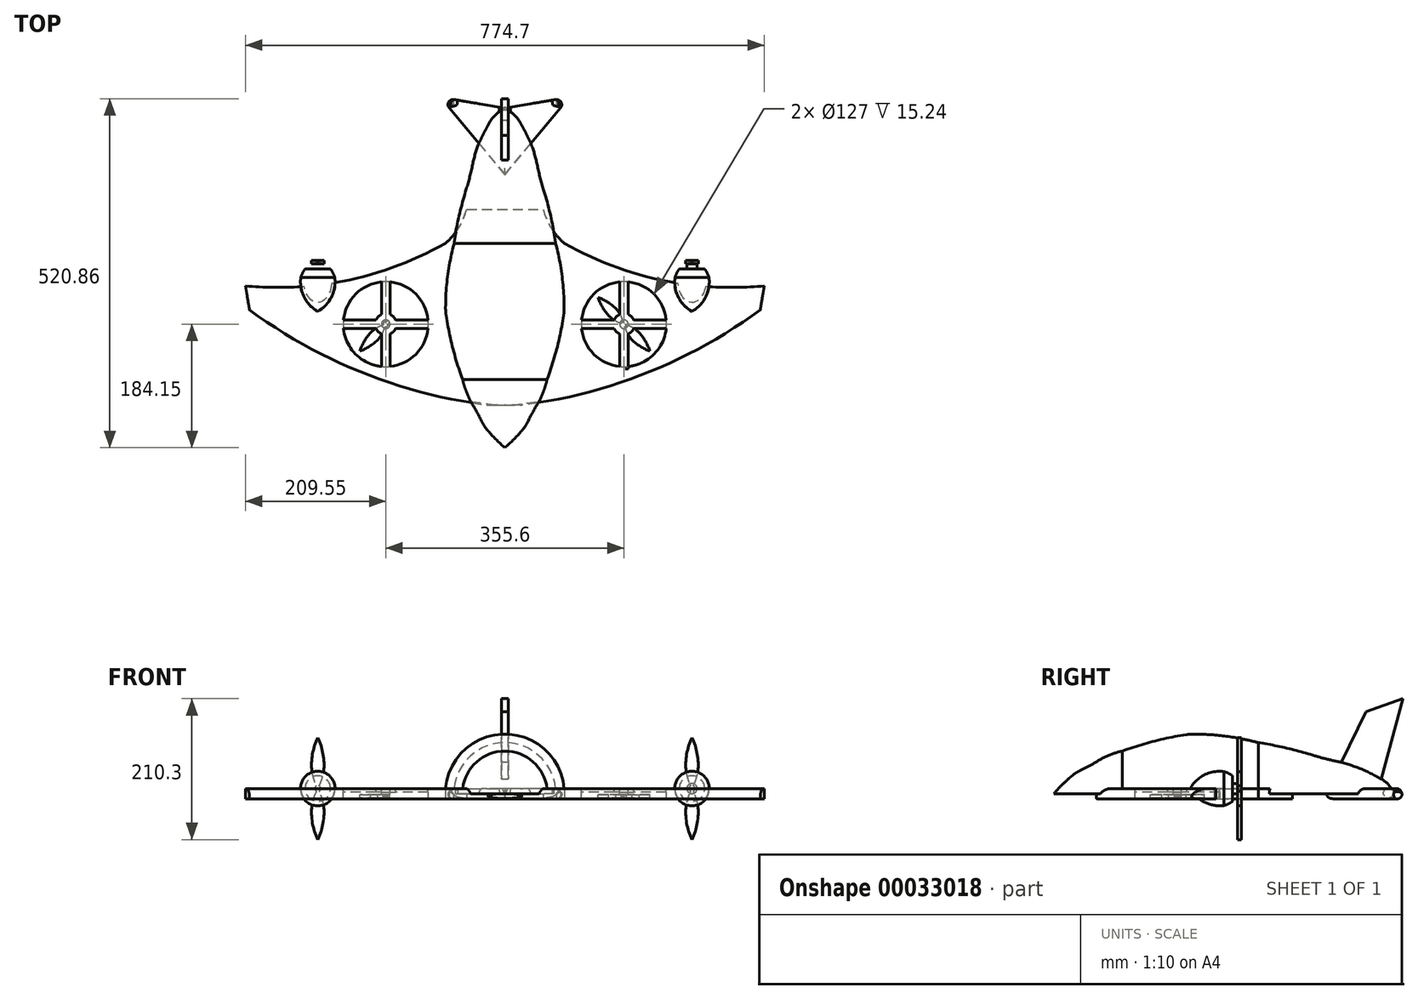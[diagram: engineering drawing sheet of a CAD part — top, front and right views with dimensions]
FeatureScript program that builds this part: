
annotation { "Feature Type Name" : "Feature", "Feature Type Description" : "" }
export const myFeature = defineFeature(function(context is Context, id is Id, definition is map)
    precondition{}
    {
        {
            var Q0;
            Q0=qCreatedBy(makeId("Top.planeOp"),FACE);
            var sketch = newSketch(context, id + "F0", { "sketchPlane" : qUnion([Q0])});
            skPoint(sketch, "E0", {"position": v(0, 304.8) * mm});
            skPoint(sketch, "E1", {"position": v(0, 203.2) * mm});
            skPoint(sketch, "E2", {"position": v(0, 101.6) * mm});
            skPoint(sketch, "E3", {"position": v(0, -101.6) * mm});
            skPoint(sketch, "E4", {"position": v(0, -152.4) * mm});
            skPoint(sketch, "E5", {"position": v(0, -203.2) * mm});
            skPoint(sketch, "E6", {"position": v(-38.1, -152.4) * mm});
            skPoint(sketch, "E7", {"position": v(38.1, -152.4) * mm});
            skPoint(sketch, "E8", {"position": v(-63.5, -101.6) * mm});
            skPoint(sketch, "E9", {"position": v(63.5, -101.6) * mm});
            skPoint(sketch, "E10", {"position": v(-88.9, 0) * mm});
            skPoint(sketch, "E11", {"position": v(88.9, 0) * mm});
            skPoint(sketch, "E12", {"position": v(-76.2, 101.6) * mm});
            skPoint(sketch, "E13", {"position": v(76.2, 101.6) * mm});
            skPoint(sketch, "E14", {"position": v(-50.8, 203.2) * mm});
            skPoint(sketch, "E15", {"position": v(50.8, 203.2) * mm});
            skPoint(sketch, "E16", {"position": v(0, -177.8) * mm});
            skPoint(sketch, "E17", {"position": v(-25.4, -177.8) * mm});
            skPoint(sketch, "E18", {"position": v(25.4, -177.8) * mm});
            skPoint(sketch, "E19", {"position": v(0, 279.4) * mm});
            skPoint(sketch, "E20", {"position": v(-25.4, 279.4) * mm});
            skPoint(sketch, "E21", {"position": v(25.4, 279.4) * mm});
            skArc(sketch, "E22", {"start": v(0, 304.8) * mm, "mid": v(-14.04, 295.38) * mm, "end": v(-24.2, 281.87) * mm});
            skArc(sketch, "E23", {"start": v(24.2, 281.87) * mm, "mid": v(14.04, 295.38) * mm, "end": v(0, 304.8) * mm});
            skArc(sketch, "E24", {"start": v(-27.7, 275.29) * mm, "mid": v(-40, 248.01) * mm, "end": v(-48.17, 219.22) * mm});
            skArc(sketch, "E25", {"start": v(48.17, 219.22) * mm, "mid": v(40, 248.01) * mm, "end": v(27.7, 275.29) * mm});
            skArc(sketch, "E26", {"start": v(-57.48, 183.04) * mm, "mid": v(-68.36, 142.67) * mm, "end": v(-76.2, 101.6) * mm});
            skArc(sketch, "E27", {"start": v(76.2, 101.6) * mm, "mid": v(68.36, 142.67) * mm, "end": v(57.48, 183.04) * mm});
            skArc(sketch, "E28", {"start": v(88.92, 5.93) * mm, "mid": v(85.6, 54.17) * mm, "end": v(76.2, 101.6) * mm});
            skArc(sketch, "E29", {"start": v(-76.2, 101.6) * mm, "mid": v(-85.6, 54.17) * mm, "end": v(-88.92, 5.93) * mm});
            skArc(sketch, "E30", {"start": v(-88.08, -5.72) * mm, "mid": v(-78.26, -54.3) * mm, "end": v(-63.5, -101.6) * mm});
            skArc(sketch, "E31", {"start": v(-23.56, -180.01) * mm, "mid": v(-12.32, -192.16) * mm, "end": v(0, -203.2) * mm});
            skArc(sketch, "E32", {"start": v(63.5, -101.6) * mm, "mid": v(78.26, -54.3) * mm, "end": v(88.08, -5.72) * mm});
            skArc(sketch, "E33", {"start": v(49.61, -136.58) * mm, "mid": v(58, -119.66) * mm, "end": v(63.5, -101.6) * mm});
            skArc(sketch, "E34", {"start": v(-63.5, -101.6) * mm, "mid": v(-58, -119.66) * mm, "end": v(-49.61, -136.58) * mm});
            skArc(sketch, "E35", {"start": v(-33.73, -165.67) * mm, "mid": v(-30.5, -171.31) * mm, "end": v(-26.57, -176.5) * mm});
            skArc(sketch, "E36", {"start": v(0, -203.2) * mm, "mid": v(12.32, -192.16) * mm, "end": v(23.56, -180.01) * mm});
            skArc(sketch, "E37", {"start": v(26.57, -176.5) * mm, "mid": v(30.5, -171.31) * mm, "end": v(33.73, -165.67) * mm});
            skLineSegment(sketch, "E38", {"start": v(0, -203.2) * mm, "end": v(0, 304.8) * mm});
            skArc(sketch, "E39.filletArc", {"start": v(-88.92, 5.93) * mm, "mid": v(-88.72, 0.09) * mm, "end": v(-88.08, -5.72) * mm});
            skArc(sketch, "E40.filletArc", {"start": v(88.08, -5.72) * mm, "mid": v(88.72, 0.09) * mm, "end": v(88.92, 5.93) * mm});
            skArc(sketch, "E41.filletArc", {"start": v(-33.73, -165.67) * mm, "mid": v(-41.35, -150.95) * mm, "end": v(-49.61, -136.58) * mm});
            skArc(sketch, "E42.filletArc", {"start": v(49.61, -136.58) * mm, "mid": v(41.35, -150.95) * mm, "end": v(33.73, -165.67) * mm});
            skArc(sketch, "E43.filletArc", {"start": v(26.57, -176.5) * mm, "mid": v(25.06, -178.25) * mm, "end": v(23.56, -180.01) * mm});
            skArc(sketch, "E44.filletArc", {"start": v(-23.56, -180.01) * mm, "mid": v(-25.06, -178.25) * mm, "end": v(-26.57, -176.5) * mm});
            skArc(sketch, "E45.filletArc", {"start": v(-57.48, 183.04) * mm, "mid": v(-52.38, 201.02) * mm, "end": v(-48.17, 219.22) * mm});
            skArc(sketch, "E46.filletArc", {"start": v(48.17, 219.22) * mm, "mid": v(52.38, 201.02) * mm, "end": v(57.48, 183.04) * mm});
            skArc(sketch, "E47.filletArc", {"start": v(-27.7, 275.29) * mm, "mid": v(-25.93, 278.57) * mm, "end": v(-24.2, 281.87) * mm});
            skArc(sketch, "E48.filletArc", {"start": v(24.2, 281.87) * mm, "mid": v(25.93, 278.57) * mm, "end": v(27.7, 275.29) * mm});
            skSolve(sketch);
        }
        {
            var Q0;
            Q0=makeQuery(id+"F0.imprint","IMPRINT",FACE,{"disambiguationData":[TD([[makeQuery(id+"F0.imprint","IMPRINT",EDGE,{"derivedFrom":sQuery(id+"F0.wireOp",EDGE,"E23")}),1.0]])]});
            var Q1;
            Q1=sQuery(id+"F0.wireOp",EDGE,"E38");
            revolve(context, id + "F1", {"entities" : qUnion([Q0]), "axis" : qUnion([Q1]), "revolveType" : RevolveType.ONE_DIRECTION, "oppositeDirection" : true, "angle" : 180 * degree});
        }
        {
            var Q0;
            Q0=qCreatedBy(makeId("Top.planeOp"),FACE);
            var sketch = newSketch(context, id + "F2", { "sketchPlane" : qUnion([Q0])});
            skPoint(sketch, "E49", {"position": v(-381, 0) * mm});
            skPoint(sketch, "E50", {"position": v(381, 0) * mm});
            skLineSegment(sketch, "E51", {"start": v(0, 0) * mm, "end": v(0, -139.7) * mm});
            skPoint(sketch, "E52", {"position": v(-38.1, -139.7) * mm});
            skPoint(sketch, "E53", {"position": v(38.1, -139.7) * mm});
            skArc(sketch, "E54", {"start": v(-381, 0) * mm, "mid": v(-218.16, -91) * mm, "end": v(-38.1, -139.7) * mm});
            skArc(sketch, "E55", {"start": v(38.1, -139.7) * mm, "mid": v(218.16, -91) * mm, "end": v(381, 0) * mm});
            skLineSegment(sketch, "E56", {"start": v(387.35, 38.1) * mm, "end": v(381, 0) * mm});
            skLineSegment(sketch, "E57", {"start": v(0, 0) * mm, "end": v(0, 152.4) * mm});
            skPoint(sketch, "E58", {"position": v(-57.15, 152.4) * mm});
            skPoint(sketch, "E59", {"position": v(57.15, 152.4) * mm});
            skPoint(sketch, "E60", {"position": v(-88.9, 0) * mm});
            skPoint(sketch, "E61", {"position": v(88.9, 0) * mm});
            skPoint(sketch, "E62", {"position": v(-88.9, 101.6) * mm});
            skPoint(sketch, "E63", {"position": v(88.9, 101.6) * mm});
            skArc(sketch, "E64", {"start": v(-88.9, 101.6) * mm, "mid": v(-69.1, 124.54) * mm, "end": v(-57.15, 152.4) * mm});
            skLineSegment(sketch, "E65", {"start": v(-38.1, -139.7) * mm, "end": v(38.1, -139.7) * mm});
            skLineSegment(sketch, "E66", {"start": v(-57.15, 152.4) * mm, "end": v(57.15, 152.4) * mm});
            skArc(sketch, "E67", {"start": v(57.15, 152.4) * mm, "mid": v(69.2, 124.6) * mm, "end": v(88.9, 101.6) * mm});
            skLineSegment(sketch, "E68", {"start": v(387.35, 0) * mm, "end": v(381, 0) * mm});
            skLineSegment(sketch, "E69", {"start": v(-381, 0) * mm, "end": v(-387.35, 0) * mm});
            skLineSegment(sketch, "E70", {"start": v(-387.35, 38.1) * mm, "end": v(-381, 0) * mm});
            skArc(sketch, "E71", {"start": v(-387.35, 38.1) * mm, "mid": v(-233.24, 46.91) * mm, "end": v(-88.9, 101.6) * mm});
            skArc(sketch, "E72", {"start": v(88.9, 101.6) * mm, "mid": v(233.24, 46.91) * mm, "end": v(387.35, 38.1) * mm});
            skSolve(sketch);
        }
        {
            var Q0;
            Q0 = qSketchRegion(id + "F2", true);
            extrude(context, id + "F3", {"entities" : qUnion([Q0]), "operationType" : NewBodyOperationType.ADD, "endBound" : BoundingType.SYMMETRIC, "depth" : 15.24 * mm});
        }
        {
            var Q0;
            Q0=qCreatedBy(makeId("Right.planeOp"),FACE);
            var sketch = newSketch(context, id + "F4", { "sketchPlane" : qUnion([Q0])});
            skLineSegment(sketch, "E73", {"start": v(0, 0) * mm, "end": v(304.8, 0) * mm});
            skLineSegment(sketch, "E74", {"start": v(0, 0) * mm, "end": v(-203.2, 0) * mm});
            skArc(sketch, "E75", {"start": v(-11.45, 37.92) * mm, "mid": v(-109.64, 30.66) * mm, "end": v(-203.2, 0) * mm});
            skArc(sketch, "E76", {"start": v(304.8, 0) * mm, "mid": v(161.16, 26.9) * mm, "end": v(15.38, 37.11) * mm});
            skPoint(sketch, "E77.visualSharp", {"position": v(0, 37.21) * mm});
            skArc(sketch, "E77.filletArc", {"start": v(-11.45, 37.92) * mm, "mid": v(1.96, 37.4) * mm, "end": v(15.38, 37.11) * mm});
            skSolve(sketch);
        }
        {
            var Q0;
            {var subQ0=sQuery(id+"F2.wireOp",EDGE,"E55");var subQ1=sQuery(id+"F2.wireOp",EDGE,"E56");var subQ2=sQuery(id+"F2.wireOp",EDGE,"E67");var subQ3=sQuery(id+"F2.wireOp",EDGE,"E72");Q0=makeQuery(id+"F3.boolean.opBoolean","SPLIT",FACE,{"disambiguationData":[TD([makeQuery(id+"F3.opExtrude","SWEPT_FACE",FACE,{"disambiguationData":[OSD([subQ0])]})])],"derivedFrom":makeQuery(id+"F3.opExtrude","CAP_FACE",FACE,{"disambiguationData":[OSD([sQuery(id+"F2.wireOp",EDGE,"E54"),subQ0,subQ1,sQuery(id+"F2.wireOp",EDGE,"E64"),sQuery(id+"F2.wireOp",EDGE,"E65"),sQuery(id+"F2.wireOp",EDGE,"E66"),subQ2,sQuery(id+"F2.wireOp",EDGE,"E70"),sQuery(id+"F2.wireOp",EDGE,"E71"),subQ3])],"isStart":false})});}
            cPlane(context, id + "F5", {"entities" : qUnion([Q0]), "cplaneType" : CPlaneType.OFFSET, "offset" : 0 * mm, "width" : 152.4 * mm, "height" : 152.4 * mm});
        }
        {
            var Q0;
            Q0=qCreatedBy(id+"F5.planeOp",FACE);
            var sketch = newSketch(context, id + "F6", { "sketchPlane" : qUnion([Q0])});
            skLineSegment(sketch, "E78", {"start": v(0, 0) * mm, "end": v(0, -19.05) * mm});
            skLineSegment(sketch, "E79", {"start": v(0, -19.05) * mm, "end": v(177.8, -19.05) * mm});
            skLineSegment(sketch, "E80", {"start": v(0, -19.05) * mm, "end": v(-177.8, -19.05) * mm});
            skCircle(sketch, "E81", {"center": v(-177.8, -19.05) * mm, "radius": 63.5 * mm});
            skCircle(sketch, "E82", {"center": v(177.8, -19.05) * mm, "radius": 63.5 * mm});
            skSolve(sketch);
        }
        {
            var Q0;
            Q0=makeQuery(id+"F3.opExtrude","CAP_EDGE",EDGE,{"disambiguationData":[OSD([sQuery(id+"F2.wireOp",EDGE,"E55")])],"isStart":false});
            var Q1;
            Q1=makeQuery(id+"F3.opExtrude","CAP_EDGE",EDGE,{"disambiguationData":[OSD([sQuery(id+"F2.wireOp",EDGE,"E54")])],"isStart":false});
            fillet(context, id + "F7", {"entities" : qUnion([Q0, Q1]), "radius" : 19.05 * mm, "allowEdgeOverflow" : false});
        }
        {
            var Q0;
            {var subQ0=sQuery(id+"F2.wireOp",EDGE,"E54");Q0=makeQuery(id+"F7.opFillet","BLEND_EDGE",EDGE,{"blendedFrom":[makeQuery(id+"F3.opExtrude","CAP_EDGE",EDGE,{"disambiguationData":[OSD([subQ0])],"isStart":false}),makeQuery(id+"F3.opExtrude","CAP_FACE",FACE,{"disambiguationData":[OSD([subQ0,sQuery(id+"F2.wireOp",EDGE,"E55"),sQuery(id+"F2.wireOp",EDGE,"E56"),sQuery(id+"F2.wireOp",EDGE,"E64"),sQuery(id+"F2.wireOp",EDGE,"E65"),sQuery(id+"F2.wireOp",EDGE,"E66"),sQuery(id+"F2.wireOp",EDGE,"E67"),sQuery(id+"F2.wireOp",EDGE,"E70"),sQuery(id+"F2.wireOp",EDGE,"E71"),sQuery(id+"F2.wireOp",EDGE,"E72")])],"isStart":true})],"blendedInto":[makeQuery(id+"F3.opExtrude","CAP_FACE",FACE,{"disambiguationData":[OSD([subQ0,sQuery(id+"F2.wireOp",EDGE,"E55"),sQuery(id+"F2.wireOp",EDGE,"E56"),sQuery(id+"F2.wireOp",EDGE,"E64"),sQuery(id+"F2.wireOp",EDGE,"E65"),sQuery(id+"F2.wireOp",EDGE,"E66"),sQuery(id+"F2.wireOp",EDGE,"E67"),sQuery(id+"F2.wireOp",EDGE,"E70"),sQuery(id+"F2.wireOp",EDGE,"E71"),sQuery(id+"F2.wireOp",EDGE,"E72")])],"isStart":true})]});}
            var Q1;
            {var subQ0=sQuery(id+"F2.wireOp",EDGE,"E55");Q1=makeQuery(id+"F7.opFillet","BLEND_EDGE",EDGE,{"blendedFrom":[makeQuery(id+"F3.opExtrude","CAP_EDGE",EDGE,{"disambiguationData":[OSD([subQ0])],"isStart":false}),makeQuery(id+"F3.opExtrude","CAP_FACE",FACE,{"disambiguationData":[OSD([sQuery(id+"F2.wireOp",EDGE,"E54"),subQ0,sQuery(id+"F2.wireOp",EDGE,"E56"),sQuery(id+"F2.wireOp",EDGE,"E64"),sQuery(id+"F2.wireOp",EDGE,"E65"),sQuery(id+"F2.wireOp",EDGE,"E66"),sQuery(id+"F2.wireOp",EDGE,"E67"),sQuery(id+"F2.wireOp",EDGE,"E70"),sQuery(id+"F2.wireOp",EDGE,"E71"),sQuery(id+"F2.wireOp",EDGE,"E72")])],"isStart":true})],"blendedInto":[makeQuery(id+"F3.opExtrude","CAP_FACE",FACE,{"disambiguationData":[OSD([sQuery(id+"F2.wireOp",EDGE,"E54"),subQ0,sQuery(id+"F2.wireOp",EDGE,"E56"),sQuery(id+"F2.wireOp",EDGE,"E64"),sQuery(id+"F2.wireOp",EDGE,"E65"),sQuery(id+"F2.wireOp",EDGE,"E66"),sQuery(id+"F2.wireOp",EDGE,"E67"),sQuery(id+"F2.wireOp",EDGE,"E70"),sQuery(id+"F2.wireOp",EDGE,"E71"),sQuery(id+"F2.wireOp",EDGE,"E72")])],"isStart":true})]});}
            fillet(context, id + "F8", {"entities" : qUnion([Q0, Q1]), "radius" : 3.8 * mm, "tangentPropagation" : true, "allowEdgeOverflow" : false});
        }
        {
            var Q0;
            Q0=sQuery(id+"F6.wireOp",VERTEX,"E81.center");
            var Q1;
            Q1=sQuery(id+"F6.wireOp",VERTEX,"E82.center");
            var Q2;
            Q2=makeQuery(id+"F1.opRevolve","SWEPT_BODY",BODY,{"disambiguationData":[OSD([sQuery(id+"F0.wireOp",EDGE,"E23"),sQuery(id+"F0.wireOp",EDGE,"E25"),sQuery(id+"F0.wireOp",EDGE,"E27"),sQuery(id+"F0.wireOp",EDGE,"E28"),sQuery(id+"F0.wireOp",EDGE,"E32"),sQuery(id+"F0.wireOp",EDGE,"E33"),sQuery(id+"F0.wireOp",EDGE,"E36"),sQuery(id+"F0.wireOp",EDGE,"E37"),sQuery(id+"F0.wireOp",EDGE,"E38"),sQuery(id+"F0.wireOp",EDGE,"E40.filletArc"),sQuery(id+"F0.wireOp",EDGE,"E42.filletArc"),sQuery(id+"F0.wireOp",EDGE,"E43.filletArc"),sQuery(id+"F0.wireOp",EDGE,"E46.filletArc"),sQuery(id+"F0.wireOp",EDGE,"E48.filletArc")])]});
            hole(context, id + "F9", {"style" : HoleStyle.SIMPLE, "holeDiameter" : 127 * mm, "endStyle" : HoleEndStyle.THROUGH, "locations" : qUnion([Q0, Q1]), "scope" : qUnion([Q2])});
        }
        {
            var Q0;
            {var subQ0=sQuery(id+"F2.wireOp",EDGE,"E54");var subQ1=sQuery(id+"F2.wireOp",EDGE,"E64");var subQ2=sQuery(id+"F2.wireOp",EDGE,"E70");var subQ3=sQuery(id+"F2.wireOp",EDGE,"E71");Q0=makeQuery(id+"F3.boolean.opBoolean","SPLIT",FACE,{"disambiguationData":[TD([makeQuery(id+"F3.opExtrude","SWEPT_FACE",FACE,{"disambiguationData":[OSD([subQ0])]})])],"derivedFrom":makeQuery(id+"F3.opExtrude","CAP_FACE",FACE,{"disambiguationData":[OSD([subQ0,sQuery(id+"F2.wireOp",EDGE,"E55"),sQuery(id+"F2.wireOp",EDGE,"E56"),subQ1,sQuery(id+"F2.wireOp",EDGE,"E65"),sQuery(id+"F2.wireOp",EDGE,"E66"),sQuery(id+"F2.wireOp",EDGE,"E67"),subQ2,subQ3,sQuery(id+"F2.wireOp",EDGE,"E72")])],"isStart":false})});}
            var sketch = newSketch(context, id + "F10", { "sketchPlane" : qUnion([Q0])});
            skPoint(sketch, "E83", {"position": v(-177.8, -19.05) * mm});
            skPoint(sketch, "E84", {"position": v(177.8, -19.05) * mm});
            skLineSegment(sketch, "E85.rect.bottom", {"start": v(-184.15, 47.62) * mm, "end": v(-171.45, 47.62) * mm});
            skLineSegment(sketch, "E85.rect.top", {"start": v(-184.15, -85.73) * mm, "end": v(-171.45, -85.73) * mm});
            skLineSegment(sketch, "E85.rect.left", {"start": v(-184.15, 47.62) * mm, "end": v(-184.15, -4.5) * mm});
            skLineSegment(sketch, "E85.rect.right", {"start": v(-171.45, 47.62) * mm, "end": v(-171.45, -4.5) * mm});
            skLineSegment(sketch, "E86.rect.bottom", {"start": v(-111.12, -25.4) * mm, "end": v(-163.25, -25.4) * mm});
            skLineSegment(sketch, "E86.rect.top", {"start": v(-111.12, -12.7) * mm, "end": v(-163.25, -12.7) * mm});
            skLineSegment(sketch, "E86.rect.left", {"start": v(-111.12, -25.4) * mm, "end": v(-111.12, -12.7) * mm});
            skLineSegment(sketch, "E86.rect.right", {"start": v(-244.48, -25.4) * mm, "end": v(-244.48, -12.7) * mm});
            skLineSegment(sketch, "E87.rect.bottom", {"start": v(244.48, -12.7) * mm, "end": v(192.35, -12.7) * mm});
            skLineSegment(sketch, "E87.rect.top", {"start": v(244.48, -25.4) * mm, "end": v(192.35, -25.4) * mm});
            skLineSegment(sketch, "E87.rect.left", {"start": v(244.48, -12.7) * mm, "end": v(244.48, -25.4) * mm});
            skLineSegment(sketch, "E87.rect.right", {"start": v(111.12, -12.7) * mm, "end": v(111.12, -25.4) * mm});
            skLineSegment(sketch, "E88.rect.bottom", {"start": v(184.15, 47.63) * mm, "end": v(171.45, 47.63) * mm});
            skLineSegment(sketch, "E88.rect.top", {"start": v(184.15, -85.73) * mm, "end": v(171.45, -85.73) * mm});
            skLineSegment(sketch, "E88.rect.left", {"start": v(184.15, 47.63) * mm, "end": v(184.15, -4.5) * mm});
            skLineSegment(sketch, "E88.rect.right", {"start": v(171.45, 47.63) * mm, "end": v(171.45, -4.5) * mm});
            skArc(sketch, "E89", {"start": v(-184.15, -4.5) * mm, "mid": v(-189.03, -7.82) * mm, "end": v(-192.35, -12.7) * mm});
            skArc(sketch, "E90", {"start": v(171.45, -4.5) * mm, "mid": v(166.57, -7.82) * mm, "end": v(163.25, -12.7) * mm});
            skLineSegment(sketch, "E91.trimOffspring", {"start": v(-192.35, -25.4) * mm, "end": v(-244.48, -25.4) * mm});
            skLineSegment(sketch, "E92.trimOffspring", {"start": v(-184.15, -33.6) * mm, "end": v(-184.15, -85.73) * mm});
            skLineSegment(sketch, "E93.trimOffspring", {"start": v(-171.45, -33.6) * mm, "end": v(-171.45, -85.73) * mm});
            skLineSegment(sketch, "E94.trimOffspring", {"start": v(-192.35, -12.7) * mm, "end": v(-244.48, -12.7) * mm});
            skArc(sketch, "E95.trimOffspring", {"start": v(-192.35, -25.4) * mm, "mid": v(-189.03, -30.28) * mm, "end": v(-184.15, -33.6) * mm});
            skArc(sketch, "E96.trimOffspring", {"start": v(-163.25, -12.7) * mm, "mid": v(-166.57, -7.82) * mm, "end": v(-171.45, -4.5) * mm});
            skArc(sketch, "E97.trimOffspring", {"start": v(-171.45, -33.6) * mm, "mid": v(-166.57, -30.28) * mm, "end": v(-163.25, -25.4) * mm});
            skLineSegment(sketch, "E98.trimOffspring", {"start": v(171.45, -33.6) * mm, "end": v(171.45, -85.73) * mm});
            skLineSegment(sketch, "E99.trimOffspring", {"start": v(163.25, -12.7) * mm, "end": v(111.12, -12.7) * mm});
            skLineSegment(sketch, "E100.trimOffspring", {"start": v(184.15, -33.6) * mm, "end": v(184.15, -85.73) * mm});
            skLineSegment(sketch, "E101.trimOffspring", {"start": v(163.25, -25.4) * mm, "end": v(111.12, -25.4) * mm});
            skArc(sketch, "E102.trimOffspring", {"start": v(184.15, -33.6) * mm, "mid": v(189.03, -30.28) * mm, "end": v(192.35, -25.4) * mm});
            skArc(sketch, "E103.trimOffspring", {"start": v(163.25, -25.4) * mm, "mid": v(166.57, -30.28) * mm, "end": v(171.45, -33.6) * mm});
            skArc(sketch, "E104.trimOffspring", {"start": v(192.35, -12.7) * mm, "mid": v(189.03, -7.82) * mm, "end": v(184.15, -4.5) * mm});
            skSolve(sketch);
        }
        {
            var Q0;
            {var subQ17=sQuery(id+"F10.wireOp",EDGE,"E89");Q0=makeQuery(id+"F10.imprint","IMPRINT",FACE,{"disambiguationData":[TD([[makeQuery(id+"F10.imprint","IMPRINT",EDGE,{"derivedFrom":subQ17}),1.0]])]});}
            var Q1;
            Q1=makeQuery(id+"F10.imprint","IMPRINT",FACE,{"disambiguationData":[TD([[makeQuery(id+"F10.imprint","IMPRINT",EDGE,{"derivedFrom":sQuery(id+"F10.wireOp",EDGE,"E87.rect.bottom")}),1.0]])]});
            extrude(context, id + "F11", {"entities" : qUnion([Q0, Q1]), "operationType" : NewBodyOperationType.ADD, "oppositeDirection" : true, "depth" : 5.08 * mm});
        }
        {
            var Q0;
            Q0=makeQuery(id+"F11.opExtrude","CAP_FACE",FACE,{"disambiguationData":[OSD([sQuery(id+"F9.hole-0.sketch.wireOp",EDGE,"core_line_2"),sQuery(id+"F9.hole-0.sketch.wireOp",EDGE,"core_line_3"),sQuery(id+"F10.wireOp",EDGE,"E85.rect.left"),sQuery(id+"F10.wireOp",EDGE,"E85.rect.right"),sQuery(id+"F10.wireOp",EDGE,"E86.rect.bottom"),sQuery(id+"F10.wireOp",EDGE,"E86.rect.top"),sQuery(id+"F10.wireOp",EDGE,"E89"),sQuery(id+"F10.wireOp",EDGE,"E91.trimOffspring"),sQuery(id+"F10.wireOp",EDGE,"E92.trimOffspring"),sQuery(id+"F10.wireOp",EDGE,"E93.trimOffspring"),sQuery(id+"F10.wireOp",EDGE,"E94.trimOffspring"),sQuery(id+"F10.wireOp",EDGE,"E95.trimOffspring"),sQuery(id+"F10.wireOp",EDGE,"E96.trimOffspring"),sQuery(id+"F10.wireOp",EDGE,"E97.trimOffspring")])],"isStart":false});
            var sketch = newSketch(context, id + "F12", { "sketchPlane" : qUnion([Q0])});
            skCircle(sketch, "E105", {"center": v(-177.8, 19.05) * mm, "radius": 6.35 * mm});
            skCircle(sketch, "E106", {"center": v(177.8, 19.05) * mm, "radius": 6.35 * mm});
            skSolve(sketch);
        }
        {
            var Q0;
            Q0 = qSketchRegion(id + "F12", true);
            extrude(context, id + "F13", {"entities" : qUnion([Q0]), "operationType" : NewBodyOperationType.ADD, "depth" : 3.8 * mm});
        }
        {
            var Q0;
            Q0=makeQuery(id+"F13.opExtrude","CAP_FACE",FACE,{"disambiguationData":[OSD([sQuery(id+"F12.wireOp",EDGE,"E105")])],"isStart":false});
            var sketch = newSketch(context, id + "F14", { "sketchPlane" : qUnion([Q0])});
            skCircle(sketch, "E107", {"center": v(-177.8, 19.05) * mm, "radius": 3.8 * mm});
            skLineSegment(sketch, "E108", {"start": v(-177.8, 19.05) * mm, "end": v(-216.58, 59.28) * mm});
            skArc(sketch, "E109", {"start": v(-216.58, 59.28) * mm, "mid": v(-209.99, 44.8) * mm, "end": v(-200.74, 31.87) * mm});
            skArc(sketch, "E110", {"start": v(-200.74, 31.87) * mm, "mid": v(-190.11, 23.95) * mm, "end": v(-177.8, 19.05) * mm});
            skLineSegment(sketch, "E111", {"start": v(-200.74, 31.87) * mm, "end": v(-189.77, 42.44) * mm});
            skPoint(sketch, "E112", {"position": v(-195.25, 37.15) * mm});
            skArc(sketch, "E113", {"start": v(-189.77, 42.44) * mm, "mid": v(-202.36, 52.16) * mm, "end": v(-216.58, 59.28) * mm});
            skArc(sketch, "E114", {"start": v(-177.8, 19.05) * mm, "mid": v(-182.24, 31.53) * mm, "end": v(-189.77, 42.44) * mm});
            skLineSegment(sketch, "E115", {"start": v(-177.8, 19.05) * mm, "end": v(-152.9, 43.06) * mm});
            skArc(sketch, "E116.MirrorCS", {"start": v(-177.8, 19.05) * mm, "mid": v(-165.49, 14.15) * mm, "end": v(-154.86, 6.23) * mm});
            skArc(sketch, "E117.MirrorCS", {"start": v(-165.83, -4.34) * mm, "mid": v(-173.36, 6.57) * mm, "end": v(-177.8, 19.05) * mm});
            skArc(sketch, "E118.MirrorCS", {"start": v(-139.02, -21.18) * mm, "mid": v(-153.24, -14.06) * mm, "end": v(-165.83, -4.34) * mm});
            skArc(sketch, "E119.MirrorCS", {"start": v(-154.86, 6.23) * mm, "mid": v(-145.61, -6.7) * mm, "end": v(-139.02, -21.18) * mm});
            skLineSegment(sketch, "E120", {"start": v(0, 0) * mm, "end": v(0, 29.33) * mm});
            skCircle(sketch, "E121.MirrorC", {"center": v(177.8, 19.05) * mm, "radius": 3.8 * mm});
            skArc(sketch, "E122.MirrorCS", {"start": v(177.8, 19.05) * mm, "mid": v(165.49, 14.15) * mm, "end": v(154.86, 6.23) * mm});
            skArc(sketch, "E123.MirrorCS", {"start": v(165.83, -4.34) * mm, "mid": v(173.36, 6.57) * mm, "end": v(177.8, 19.05) * mm});
            skArc(sketch, "E124.MirrorCS", {"start": v(139.02, -21.18) * mm, "mid": v(153.24, -14.06) * mm, "end": v(165.83, -4.34) * mm});
            skArc(sketch, "E125.MirrorCS", {"start": v(154.86, 6.23) * mm, "mid": v(145.61, -6.7) * mm, "end": v(139.02, -21.18) * mm});
            skArc(sketch, "E126.MirrorCS", {"start": v(177.8, 19.05) * mm, "mid": v(182.24, 31.53) * mm, "end": v(189.77, 42.44) * mm});
            skArc(sketch, "E127.MirrorCS", {"start": v(200.74, 31.87) * mm, "mid": v(190.11, 23.95) * mm, "end": v(177.8, 19.05) * mm});
            skArc(sketch, "E128.MirrorCS", {"start": v(216.58, 59.28) * mm, "mid": v(209.99, 44.8) * mm, "end": v(200.74, 31.87) * mm});
            skArc(sketch, "E129.MirrorCS", {"start": v(189.77, 42.44) * mm, "mid": v(202.36, 52.16) * mm, "end": v(216.58, 59.28) * mm});
            skSolve(sketch);
        }
        {
            var Q0;
            {var subQ1=sQuery(id+"F14.wireOp",EDGE,"E124.MirrorCS");Q0=makeQuery(id+"F14.imprint","IMPRINT",FACE,{"disambiguationData":[TD([[makeQuery(id+"F14.imprint","IMPRINT",EDGE,{"derivedFrom":subQ1}),1.0]])]});}
            var Q1;
            {var subQ1=sQuery(id+"F14.wireOp",EDGE,"E128.MirrorCS");Q1=makeQuery(id+"F14.imprint","IMPRINT",FACE,{"disambiguationData":[TD([[makeQuery(id+"F14.imprint","IMPRINT",EDGE,{"derivedFrom":subQ1}),-1.0]])]});}
            var Q2;
            {var subQ0=sQuery(id+"F14.wireOp",EDGE,"E127.MirrorCS");var subQ1=sQuery(id+"F14.wireOp",EDGE,"E121.MirrorC");var subQ2=makeQuery(id+"F14.imprint","INTERSECT",VERTEX,{"derivedFrom":[subQ1,subQ0]});Q2=makeQuery(id+"F14.imprint","IMPRINT",FACE,{"disambiguationData":[TD([[makeQuery(id+"F14.imprint","IMPRINT",EDGE,{"disambiguationData":[TD([[subQ2,-1.0]])],"derivedFrom":subQ1}),-1.0]])]});}
            var Q3;
            {var subQ0=sQuery(id+"F14.wireOp",EDGE,"E126.MirrorCS");var subQ1=sQuery(id+"F14.wireOp",EDGE,"E121.MirrorC");var subQ2=makeQuery(id+"F14.imprint","INTERSECT",VERTEX,{"derivedFrom":[subQ1,subQ0]});Q3=makeQuery(id+"F14.imprint","IMPRINT",FACE,{"disambiguationData":[TD([[makeQuery(id+"F14.imprint","IMPRINT",EDGE,{"disambiguationData":[TD([[subQ2,1.0]])],"derivedFrom":subQ1}),-1.0]])]});}
            var Q4;
            {var subQ0=sQuery(id+"F14.wireOp",EDGE,"E123.MirrorCS");var subQ1=sQuery(id+"F14.wireOp",EDGE,"E121.MirrorC");var subQ2=makeQuery(id+"F14.imprint","INTERSECT",VERTEX,{"derivedFrom":[subQ1,subQ0]});Q4=makeQuery(id+"F14.imprint","IMPRINT",FACE,{"disambiguationData":[TD([[makeQuery(id+"F14.imprint","IMPRINT",EDGE,{"disambiguationData":[TD([[subQ2,-1.0]])],"derivedFrom":subQ1}),-1.0]])]});}
            var Q5;
            {var subQ0=sQuery(id+"F14.wireOp",EDGE,"E127.MirrorCS");var subQ1=sQuery(id+"F14.wireOp",EDGE,"E121.MirrorC");var subQ2=makeQuery(id+"F14.imprint","INTERSECT",VERTEX,{"derivedFrom":[subQ1,subQ0]});Q5=makeQuery(id+"F14.imprint","IMPRINT",FACE,{"disambiguationData":[TD([[makeQuery(id+"F14.imprint","IMPRINT",EDGE,{"disambiguationData":[TD([[subQ2,1.0]])],"derivedFrom":subQ1}),-1.0]])]});}
            var Q6;
            {var subQ1=sQuery(id+"F14.wireOp",EDGE,"E108");var subQ5=sQuery(id+"F14.wireOp",EDGE,"E111");var subQ6=makeQuery(id+"F14.imprint","INTERSECT",VERTEX,{"derivedFrom":[subQ1,subQ5]});Q6=makeQuery(id+"F14.imprint","IMPRINT",FACE,{"disambiguationData":[TD([[makeQuery(id+"F14.imprint","IMPRINT",EDGE,{"disambiguationData":[TD([[subQ6,1.0]])],"derivedFrom":subQ1}),1.0]])]});}
            var Q7;
            {var subQ3=sQuery(id+"F14.wireOp",EDGE,"E109");Q7=makeQuery(id+"F14.imprint","IMPRINT",FACE,{"disambiguationData":[TD([[makeQuery(id+"F14.imprint","IMPRINT",EDGE,{"derivedFrom":subQ3}),1.0]])]});}
            var Q8;
            {var subQ0=sQuery(id+"F14.wireOp",EDGE,"E113");Q8=makeQuery(id+"F14.imprint","IMPRINT",FACE,{"disambiguationData":[TD([[makeQuery(id+"F14.imprint","IMPRINT",EDGE,{"derivedFrom":subQ0}),1.0]])]});}
            var Q9;
            {var subQ1=sQuery(id+"F14.wireOp",EDGE,"E108");var subQ5=sQuery(id+"F14.wireOp",EDGE,"E111");var subQ7=makeQuery(id+"F14.imprint","INTERSECT",VERTEX,{"derivedFrom":[subQ1,subQ5]});Q9=makeQuery(id+"F14.imprint","IMPRINT",FACE,{"disambiguationData":[TD([[makeQuery(id+"F14.imprint","IMPRINT",EDGE,{"disambiguationData":[TD([[subQ7,1.0]])],"derivedFrom":subQ1}),-1.0]])]});}
            var Q10;
            {var subQ3=sQuery(id+"F14.wireOp",EDGE,"E114");var subQ5=sQuery(id+"F14.wireOp",EDGE,"E107");var subQ6=makeQuery(id+"F14.imprint","INTERSECT",VERTEX,{"derivedFrom":[subQ5,subQ3]});Q10=makeQuery(id+"F14.imprint","IMPRINT",FACE,{"disambiguationData":[TD([[makeQuery(id+"F14.imprint","IMPRINT",EDGE,{"disambiguationData":[TD([[subQ6,-1.0]])],"derivedFrom":subQ5}),-1.0]])]});}
            var Q11;
            {var subQ3=sQuery(id+"F14.wireOp",EDGE,"E107");var subQ5=sQuery(id+"F14.wireOp",EDGE,"E108");var subQ7=makeQuery(id+"F14.imprint","INTERSECT",VERTEX,{"derivedFrom":[subQ3,subQ5]});Q11=makeQuery(id+"F14.imprint","IMPRINT",FACE,{"disambiguationData":[TD([[makeQuery(id+"F14.imprint","IMPRINT",EDGE,{"disambiguationData":[TD([[subQ7,-1.0]])],"derivedFrom":subQ3}),-1.0]])]});}
            var Q12;
            {var subQ1=sQuery(id+"F14.wireOp",EDGE,"E107");var subQ3=sQuery(id+"F14.wireOp",EDGE,"E108");var subQ5=makeQuery(id+"F14.imprint","INTERSECT",VERTEX,{"derivedFrom":[subQ1,subQ3]});Q12=makeQuery(id+"F14.imprint","IMPRINT",FACE,{"disambiguationData":[TD([[makeQuery(id+"F14.imprint","IMPRINT",EDGE,{"disambiguationData":[TD([[subQ5,-1.0]])],"derivedFrom":subQ1}),1.0]])]});}
            var Q13;
            {var subQ0=sQuery(id+"F14.wireOp",EDGE,"E114");var subQ1=sQuery(id+"F14.wireOp",EDGE,"E107");var subQ2=makeQuery(id+"F14.imprint","INTERSECT",VERTEX,{"derivedFrom":[subQ1,subQ0]});Q13=makeQuery(id+"F14.imprint","IMPRINT",FACE,{"disambiguationData":[TD([[makeQuery(id+"F14.imprint","IMPRINT",EDGE,{"disambiguationData":[TD([[subQ2,-1.0]])],"derivedFrom":subQ1}),1.0]])]});}
            var Q14;
            {var subQ1=sQuery(id+"F14.wireOp",EDGE,"E107");var subQ3=sQuery(id+"F14.wireOp",EDGE,"E110");var subQ5=makeQuery(id+"F14.imprint","INTERSECT",VERTEX,{"derivedFrom":[subQ1,subQ3]});Q14=makeQuery(id+"F14.imprint","IMPRINT",FACE,{"disambiguationData":[TD([[makeQuery(id+"F14.imprint","IMPRINT",EDGE,{"disambiguationData":[TD([[subQ5,-1.0]])],"derivedFrom":subQ1}),1.0]])]});}
            var Q15;
            {var subQ1=sQuery(id+"F14.wireOp",EDGE,"E107");var subQ3=sQuery(id+"F14.wireOp",EDGE,"E115");var subQ5=makeQuery(id+"F14.imprint","INTERSECT",VERTEX,{"derivedFrom":[subQ1,subQ3]});Q15=makeQuery(id+"F14.imprint","IMPRINT",FACE,{"disambiguationData":[TD([[makeQuery(id+"F14.imprint","IMPRINT",EDGE,{"disambiguationData":[TD([[subQ5,1.0]])],"derivedFrom":subQ1}),1.0]])]});}
            var Q16;
            {var subQ1=sQuery(id+"F14.wireOp",EDGE,"E107");var subQ3=sQuery(id+"F14.wireOp",EDGE,"E114");var subQ5=makeQuery(id+"F14.imprint","INTERSECT",VERTEX,{"derivedFrom":[subQ1,subQ3]});Q16=makeQuery(id+"F14.imprint","IMPRINT",FACE,{"disambiguationData":[TD([[makeQuery(id+"F14.imprint","IMPRINT",EDGE,{"disambiguationData":[TD([[subQ5,1.0]])],"derivedFrom":subQ1}),1.0]])]});}
            var Q17;
            {var subQ0=sQuery(id+"F14.wireOp",EDGE,"E117.MirrorCS");var subQ1=sQuery(id+"F14.wireOp",EDGE,"E107");var subQ2=makeQuery(id+"F14.imprint","INTERSECT",VERTEX,{"derivedFrom":[subQ1,subQ0]});Q17=makeQuery(id+"F14.imprint","IMPRINT",FACE,{"disambiguationData":[TD([[makeQuery(id+"F14.imprint","IMPRINT",EDGE,{"disambiguationData":[TD([[subQ2,-1.0]])],"derivedFrom":subQ1}),1.0]])]});}
            var Q18;
            {var subQ6=sQuery(id+"F14.wireOp",EDGE,"E118.MirrorCS");Q18=makeQuery(id+"F14.imprint","IMPRINT",FACE,{"disambiguationData":[TD([[makeQuery(id+"F14.imprint","IMPRINT",EDGE,{"derivedFrom":subQ6}),-1.0]])]});}
            var Q19;
            {var subQ1=sQuery(id+"F14.wireOp",EDGE,"E117.MirrorCS");var subQ5=sQuery(id+"F14.wireOp",EDGE,"E107");var subQ6=makeQuery(id+"F14.imprint","INTERSECT",VERTEX,{"derivedFrom":[subQ5,subQ1]});Q19=makeQuery(id+"F14.imprint","IMPRINT",FACE,{"disambiguationData":[TD([[makeQuery(id+"F14.imprint","IMPRINT",EDGE,{"disambiguationData":[TD([[subQ6,-1.0]])],"derivedFrom":subQ5}),-1.0]])]});}
            extrude(context, id + "F15", {"entities" : qUnion([Q0, Q1, Q2, Q3, Q4, Q5, Q6, Q7, Q8, Q9, Q10, Q11, Q12, Q13, Q14, Q15, Q16, Q17, Q18, Q19]), "operationType" : NewBodyOperationType.ADD, "depth" : 5.08 * mm});
        }
        {
            var Q0;
            {var subQ0=sQuery(id+"F2.wireOp",EDGE,"E54");var subQ1=sQuery(id+"F2.wireOp",EDGE,"E64");var subQ2=sQuery(id+"F2.wireOp",EDGE,"E70");var subQ3=sQuery(id+"F2.wireOp",EDGE,"E71");Q0=makeQuery(id+"F11.boolean.opBoolean","MERGE",FACE,{"derivedFrom":[makeQuery(id+"F3.boolean.opBoolean","SPLIT",FACE,{"disambiguationData":[TD([makeQuery(id+"F3.opExtrude","SWEPT_FACE",FACE,{"disambiguationData":[OSD([subQ0])]})])],"derivedFrom":makeQuery(id+"F3.opExtrude","CAP_FACE",FACE,{"disambiguationData":[OSD([subQ0,sQuery(id+"F2.wireOp",EDGE,"E55"),sQuery(id+"F2.wireOp",EDGE,"E56"),subQ1,sQuery(id+"F2.wireOp",EDGE,"E65"),sQuery(id+"F2.wireOp",EDGE,"E66"),sQuery(id+"F2.wireOp",EDGE,"E67"),subQ2,subQ3,sQuery(id+"F2.wireOp",EDGE,"E72")])],"isStart":false})}),makeQuery(id+"F11.opExtrude","CAP_FACE",FACE,{"disambiguationData":[OSD([sQuery(id+"F9.hole-0.sketch.wireOp",EDGE,"core_line_2"),sQuery(id+"F9.hole-0.sketch.wireOp",EDGE,"core_line_3"),sQuery(id+"F10.wireOp",EDGE,"E85.rect.left"),sQuery(id+"F10.wireOp",EDGE,"E85.rect.right"),sQuery(id+"F10.wireOp",EDGE,"E86.rect.bottom"),sQuery(id+"F10.wireOp",EDGE,"E86.rect.top"),sQuery(id+"F10.wireOp",EDGE,"E89"),sQuery(id+"F10.wireOp",EDGE,"E91.trimOffspring"),sQuery(id+"F10.wireOp",EDGE,"E92.trimOffspring"),sQuery(id+"F10.wireOp",EDGE,"E93.trimOffspring"),sQuery(id+"F10.wireOp",EDGE,"E94.trimOffspring"),sQuery(id+"F10.wireOp",EDGE,"E95.trimOffspring"),sQuery(id+"F10.wireOp",EDGE,"E96.trimOffspring"),sQuery(id+"F10.wireOp",EDGE,"E97.trimOffspring")])],"isStart":true})]});}
            var sketch = newSketch(context, id + "F16", { "sketchPlane" : qUnion([Q0])});
            skLineSegment(sketch, "E130", {"start": v(0, 0) * mm, "end": v(-279.4, 0) * mm});
            skLineSegment(sketch, "E131", {"start": v(0, 0) * mm, "end": v(279.4, 0) * mm});
            skLineSegment(sketch, "E132", {"start": v(-279.4, 0) * mm, "end": v(-279.4, 63.5) * mm});
            skPoint(sketch, "E133", {"position": v(-279.4, 50.8) * mm});
            skLineSegment(sketch, "E134", {"start": v(-279.4, 50.8) * mm, "end": v(-304.8, 50.8) * mm});
            skLineSegment(sketch, "E135", {"start": v(-279.4, 63.5) * mm, "end": v(-298.45, 63.5) * mm});
            skArc(sketch, "E136", {"start": v(-298.45, 63.5) * mm, "mid": v(-302.07, 57.37) * mm, "end": v(-304.8, 50.8) * mm});
            skArc(sketch, "E137", {"start": v(-304.8, 50.8) * mm, "mid": v(-299.86, 21.52) * mm, "end": v(-279.4, 0) * mm});
            skLineSegment(sketch, "E138", {"start": v(0, 0) * mm, "end": v(0, 106.2) * mm});
            skLineSegment(sketch, "E139.MirrorCS", {"start": v(279.4, 0) * mm, "end": v(279.4, 63.5) * mm});
            skArc(sketch, "E140.MirrorCS", {"start": v(304.8, 50.8) * mm, "mid": v(299.86, 21.52) * mm, "end": v(279.4, 0) * mm});
            skArc(sketch, "E141.MirrorCS", {"start": v(298.45, 63.5) * mm, "mid": v(302.07, 57.37) * mm, "end": v(304.8, 50.8) * mm});
            skLineSegment(sketch, "E142.MirrorCS", {"start": v(279.4, 63.5) * mm, "end": v(298.45, 63.5) * mm});
            skSolve(sketch);
        }
        {
            var Q0;
            {var subQ0=makeQuery(id+"F3.opExtrude","CAP_EDGE",EDGE,{"disambiguationData":[OSD([sQuery(id+"F2.wireOp",EDGE,"E71")])],"isStart":false});var subQ3=sQuery(id+"F16.wireOp",EDGE,"E132");var subQ4=makeQuery(id+"F16.imprint","INTERSECT",VERTEX,{"derivedFrom":[subQ0,subQ3]});Q0=makeQuery(id+"F16.imprint","IMPRINT",FACE,{"disambiguationData":[TD([[makeQuery(id+"F16.imprint","IMPRINT",EDGE,{"disambiguationData":[TD([[subQ4,1.0]])],"derivedFrom":subQ0}),-1.0]])]});}
            var Q1;
            {var subQ5=sQuery(id+"F16.wireOp",EDGE,"E134");Q1=makeQuery(id+"F16.imprint","IMPRINT",FACE,{"disambiguationData":[TD([[makeQuery(id+"F16.imprint","IMPRINT",EDGE,{"derivedFrom":subQ5}),1.0]])]});}
            var Q2;
            {var subQ1=sQuery(id+"F16.wireOp",EDGE,"E134");Q2=makeQuery(id+"F16.imprint","IMPRINT",FACE,{"disambiguationData":[TD([[makeQuery(id+"F16.imprint","IMPRINT",EDGE,{"derivedFrom":subQ1}),-1.0]])]});}
            var Q3;
            Q3=sQuery(id+"F16.wireOp",EDGE,"E132");
            revolve(context, id + "F17", {"operationType" : NewBodyOperationType.ADD, "entities" : qUnion([Q0, Q1, Q2]), "axis" : qUnion([Q3]), "revolveType" : RevolveType.FULL});
        }
        {
            var Q0;
            {var subQ0=sQuery(id+"F2.wireOp",EDGE,"E55");var subQ1=sQuery(id+"F2.wireOp",EDGE,"E56");var subQ2=sQuery(id+"F2.wireOp",EDGE,"E67");var subQ3=sQuery(id+"F2.wireOp",EDGE,"E72");Q0=makeQuery(id+"F11.boolean.opBoolean","MERGE",FACE,{"derivedFrom":[makeQuery(id+"F3.boolean.opBoolean","SPLIT",FACE,{"disambiguationData":[TD([makeQuery(id+"F3.opExtrude","SWEPT_FACE",FACE,{"disambiguationData":[OSD([subQ0])]})])],"derivedFrom":makeQuery(id+"F3.opExtrude","CAP_FACE",FACE,{"disambiguationData":[OSD([sQuery(id+"F2.wireOp",EDGE,"E54"),subQ0,subQ1,sQuery(id+"F2.wireOp",EDGE,"E64"),sQuery(id+"F2.wireOp",EDGE,"E65"),sQuery(id+"F2.wireOp",EDGE,"E66"),subQ2,sQuery(id+"F2.wireOp",EDGE,"E70"),sQuery(id+"F2.wireOp",EDGE,"E71"),subQ3])],"isStart":false})}),makeQuery(id+"F11.opExtrude","CAP_FACE",FACE,{"disambiguationData":[OSD([sQuery(id+"F10.wireOp",EDGE,"E87.rect.bottom"),sQuery(id+"F10.wireOp",EDGE,"E87.rect.top"),sQuery(id+"F10.wireOp",EDGE,"E87.rect.left"),sQuery(id+"F10.wireOp",EDGE,"E87.rect.right"),sQuery(id+"F10.wireOp",EDGE,"E88.rect.bottom"),sQuery(id+"F10.wireOp",EDGE,"E88.rect.top"),sQuery(id+"F10.wireOp",EDGE,"E88.rect.left"),sQuery(id+"F10.wireOp",EDGE,"E88.rect.right"),sQuery(id+"F10.wireOp",EDGE,"E90"),sQuery(id+"F10.wireOp",EDGE,"E98.trimOffspring"),sQuery(id+"F10.wireOp",EDGE,"E99.trimOffspring"),sQuery(id+"F10.wireOp",EDGE,"E100.trimOffspring"),sQuery(id+"F10.wireOp",EDGE,"E101.trimOffspring"),sQuery(id+"F10.wireOp",EDGE,"E102.trimOffspring"),sQuery(id+"F10.wireOp",EDGE,"E103.trimOffspring"),sQuery(id+"F10.wireOp",EDGE,"E104.trimOffspring")])],"isStart":true})]});}
            var sketch = newSketch(context, id + "F18", { "sketchPlane" : qUnion([Q0])});
            skLineSegment(sketch, "E143", {"start": v(0, 0) * mm, "end": v(0, 145.45) * mm});
            skLineSegment(sketch, "E144", {"start": v(0, 0) * mm, "end": v(279.4, 0) * mm});
            skLineSegment(sketch, "E145", {"start": v(279.4, 0) * mm, "end": v(279.4, 63.5) * mm});
            skLineSegment(sketch, "E146", {"start": v(279.4, 63.5) * mm, "end": v(260.35, 63.5) * mm});
            skLineSegment(sketch, "E147", {"start": v(279.4, 50.8) * mm, "end": v(254, 50.8) * mm});
            skArc(sketch, "E148", {"start": v(260.35, 63.5) * mm, "mid": v(256.73, 57.37) * mm, "end": v(254, 50.8) * mm});
            skArc(sketch, "E149", {"start": v(254, 50.8) * mm, "mid": v(258.94, 21.52) * mm, "end": v(279.4, 0) * mm});
            skSolve(sketch);
        }
        {
            var Q0;
            Q0 = qSketchRegion(id + "F18", true);
            var Q1;
            Q1=sQuery(id+"F18.wireOp",EDGE,"E145");
            revolve(context, id + "F19", {"operationType" : NewBodyOperationType.ADD, "entities" : qUnion([Q0]), "axis" : qUnion([Q1]), "revolveType" : RevolveType.FULL});
        }
        {
            var Q0;
            Q0=makeQuery(id+"F19.opRevolve","SWEPT_FACE",FACE,{"disambiguationData":[OSD([sQuery(id+"F18.wireOp",EDGE,"E146")])]});
            var sketch = newSketch(context, id + "F20", { "sketchPlane" : qUnion([Q0])});
            skCircle(sketch, "E150", {"center": v(-279.4, 7.62) * mm, "radius": 7.62 * mm});
            skLineSegment(sketch, "E151", {"start": v(0, 0) * mm, "end": v(0, 114.33) * mm});
            skCircle(sketch, "E152.MirrorC", {"center": v(279.4, 7.62) * mm, "radius": 7.62 * mm});
            skSolve(sketch);
        }
        {
            var Q0;
            Q0=makeQuery(id+"F20.imprint","IMPRINT",FACE,{"disambiguationData":[TD([[makeQuery(id+"F20.imprint","IMPRINT",EDGE,{"derivedFrom":sQuery(id+"F20.wireOp",EDGE,"E150")}),1.0]])]});
            var Q1;
            Q1=makeQuery(id+"F20.imprint","IMPRINT",FACE,{"disambiguationData":[TD([[makeQuery(id+"F20.imprint","IMPRINT",EDGE,{"derivedFrom":sQuery(id+"F20.wireOp",EDGE,"E152.MirrorC")}),-1.0]])]});
            extrude(context, id + "F21", {"entities" : qUnion([Q0, Q1]), "operationType" : NewBodyOperationType.ADD, "depth" : 7.62 * mm});
        }
        {
            var Q0;
            Q0=makeQuery(id+"F21.opExtrude","CAP_FACE",FACE,{"disambiguationData":[OSD([sQuery(id+"F20.wireOp",EDGE,"E150")])],"isStart":false});
            var sketch = newSketch(context, id + "F22", { "sketchPlane" : qUnion([Q0])});
            skCircle(sketch, "E153", {"center": v(-279.4, 7.62) * mm, "radius": 4.45 * mm});
            skLineSegment(sketch, "E154", {"start": v(-279.4, 7.62) * mm, "end": v(-279.4, 83.82) * mm});
            skLineSegment(sketch, "E155", {"start": v(-279.4, 33.02) * mm, "end": v(-270.5, 33.02) * mm});
            skArc(sketch, "E156", {"start": v(-279.4, 7.62) * mm, "mid": v(-273.82, 19.92) * mm, "end": v(-270.5, 33.02) * mm});
            skArc(sketch, "E157", {"start": v(-270.5, 33.02) * mm, "mid": v(-271.45, 59.03) * mm, "end": v(-279.4, 83.82) * mm});
            skArc(sketch, "E158.MirrorCS", {"start": v(-288.29, 33.02) * mm, "mid": v(-287.35, 59.03) * mm, "end": v(-279.4, 83.82) * mm});
            skArc(sketch, "E159.MirrorCS", {"start": v(-279.4, 7.62) * mm, "mid": v(-284.98, 19.92) * mm, "end": v(-288.3, 33.02) * mm});
            skLineSegment(sketch, "E160", {"start": v(-279.4, 7.62) * mm, "end": v(-229.83, 7.62) * mm});
            skArc(sketch, "E161.MirrorCS", {"start": v(-279.4, 7.62) * mm, "mid": v(-273.82, -4.68) * mm, "end": v(-270.5, -17.78) * mm});
            skArc(sketch, "E162.MirrorCS", {"start": v(-279.4, 7.62) * mm, "mid": v(-284.98, -4.68) * mm, "end": v(-288.3, -17.78) * mm});
            skArc(sketch, "E163.MirrorCS", {"start": v(-288.29, -17.78) * mm, "mid": v(-287.35, -43.8) * mm, "end": v(-279.4, -68.58) * mm});
            skArc(sketch, "E164.MirrorCS", {"start": v(-270.5, -17.78) * mm, "mid": v(-271.45, -43.8) * mm, "end": v(-279.4, -68.58) * mm});
            skLineSegment(sketch, "E165", {"start": v(0, 0) * mm, "end": v(0, 102.9) * mm});
            skArc(sketch, "E166.MirrorCS", {"start": v(279.4, 7.62) * mm, "mid": v(284.98, 19.92) * mm, "end": v(288.3, 33.02) * mm});
            skArc(sketch, "E167.MirrorCS", {"start": v(288.29, 33.02) * mm, "mid": v(287.35, 59.03) * mm, "end": v(279.4, 83.82) * mm});
            skArc(sketch, "E168.MirrorCS", {"start": v(270.5, 33.02) * mm, "mid": v(271.45, 59.03) * mm, "end": v(279.4, 83.82) * mm});
            skArc(sketch, "E169.MirrorCS", {"start": v(279.4, 7.62) * mm, "mid": v(273.82, 19.92) * mm, "end": v(270.5, 33.02) * mm});
            skCircle(sketch, "E170.MirrorC", {"center": v(279.4, 7.62) * mm, "radius": 4.45 * mm});
            skArc(sketch, "E171.MirrorCS", {"start": v(279.4, 7.62) * mm, "mid": v(273.82, -4.68) * mm, "end": v(270.5, -17.78) * mm});
            skArc(sketch, "E172.MirrorCS", {"start": v(279.4, 7.62) * mm, "mid": v(284.98, -4.68) * mm, "end": v(288.3, -17.78) * mm});
            skArc(sketch, "E173.MirrorCS", {"start": v(288.29, -17.78) * mm, "mid": v(287.35, -43.8) * mm, "end": v(279.4, -68.58) * mm});
            skArc(sketch, "E174.MirrorCS", {"start": v(270.5, -17.78) * mm, "mid": v(271.45, -43.8) * mm, "end": v(279.4, -68.58) * mm});
            skSolve(sketch);
        }
        {
            var Q0;
            Q0 = qSketchRegion(id + "F22", true);
            var Q1;
            {var subQ0=sQuery(id+"F22.wireOp",EDGE,"E156");var subQ1=sQuery(id+"F22.wireOp",EDGE,"E153");var subQ2=makeQuery(id+"F22.imprint","INTERSECT",VERTEX,{"derivedFrom":[subQ1,subQ0]});Q1=makeQuery(id+"F22.imprint","IMPRINT",FACE,{"disambiguationData":[TD([[makeQuery(id+"F22.imprint","IMPRINT",EDGE,{"disambiguationData":[TD([[subQ2,-1.0]])],"derivedFrom":subQ1}),1.0]])]});}
            var Q2;
            {var subQ1=sQuery(id+"F22.wireOp",EDGE,"E153");var subQ3=sQuery(id+"F22.wireOp",EDGE,"E154");var subQ5=makeQuery(id+"F22.imprint","INTERSECT",VERTEX,{"derivedFrom":[subQ1,subQ3]});Q2=makeQuery(id+"F22.imprint","IMPRINT",FACE,{"disambiguationData":[TD([[makeQuery(id+"F22.imprint","IMPRINT",EDGE,{"disambiguationData":[TD([[subQ5,-1.0]])],"derivedFrom":subQ1}),1.0]])]});}
            extrude(context, id + "F23", {"entities" : qUnion([Q0, Q1, Q2]), "operationType" : NewBodyOperationType.ADD, "depth" : 5.08 * mm});
        }
        {
            var Q0;
            Q0=qCreatedBy(makeId("Right.planeOp"),FACE);
            var sketch = newSketch(context, id + "F24", { "sketchPlane" : qUnion([Q0])});
            skLineSegment(sketch, "E175", {"start": v(203.2, 0) * mm, "end": v(279.4, 0) * mm});
            skLineSegment(sketch, "E176", {"start": v(203.2, 0) * mm, "end": v(262.78, 122.51) * mm});
            skLineSegment(sketch, "E177", {"start": v(262.78, 122.51) * mm, "end": v(317.66, 141.72) * mm});
            skLineSegment(sketch, "E178", {"start": v(317.66, 141.72) * mm, "end": v(279.4, 0) * mm});
            skSolve(sketch);
        }
        {
            var Q0;
            Q0 = qSketchRegion(id + "F24", true);
            extrude(context, id + "F25", {"entities" : qUnion([Q0]), "operationType" : NewBodyOperationType.ADD, "endBound" : BoundingType.SYMMETRIC, "depth" : 10.16 * mm});
        }
        {
            var Q0;
            Q0=makeQuery(id+"F0.imprint","IMPRINT",FACE,{"disambiguationData":[TD([[makeQuery(id+"F0.imprint","IMPRINT",EDGE,{"derivedFrom":sQuery(id+"F0.wireOp",EDGE,"E22")}),1.0]])]});
            var sketch = newSketch(context, id + "F26", { "sketchPlane" : qUnion([Q0])});
            skLineSegment(sketch, "E179", {"start": v(0, 303.63) * mm, "end": v(76.2, 303.63) * mm});
            skLineSegment(sketch, "E180", {"start": v(0, 303.63) * mm, "end": v(-63.5, 303.63) * mm});
            skLineSegment(sketch, "E181", {"start": v(76.2, 303.63) * mm, "end": v(76.2, 316.33) * mm});
            skLineSegment(sketch, "E182", {"start": v(76.2, 316.33) * mm, "end": v(95.25, 316.33) * mm});
            skLineSegment(sketch, "E183", {"start": v(0, 202.03) * mm, "end": v(0, 303.63) * mm});
            skLineSegment(sketch, "E184", {"start": v(76.2, 316.33) * mm, "end": v(0, 303.63) * mm});
            skLineSegment(sketch, "E185", {"start": v(95.25, 316.33) * mm, "end": v(0, 202.03) * mm});
            skLineSegment(sketch, "E186.MirrorCS", {"start": v(-95.25, 316.33) * mm, "end": v(0, 202.03) * mm});
            skLineSegment(sketch, "E187.MirrorCS", {"start": v(-76.2, 316.33) * mm, "end": v(-95.25, 316.33) * mm});
            skLineSegment(sketch, "E188.MirrorCS", {"start": v(-76.2, 316.33) * mm, "end": v(0, 303.63) * mm});
            skSolve(sketch);
        }
        {
            var Q0;
            Q0 = qSketchRegion(id + "F26", true);
            var Q1;
            Q1=makeQuery(id+"F26.imprint","IMPRINT",FACE,{"disambiguationData":[TD([[makeQuery(id+"F26.imprint","IMPRINT",EDGE,{"derivedFrom":sQuery(id+"F26.wireOp",EDGE,"E179")}),-1.0]])]});
            extrude(context, id + "F27", {"entities" : qUnion([Q0, Q1]), "operationType" : NewBodyOperationType.ADD, "endBound" : BoundingType.SYMMETRIC, "oppositeDirection" : true, "depth" : 15.24 * mm});
        }
        {
            var Q0;
            Q0=makeQuery(id+"F27.opExtrude","CAP_EDGE",EDGE,{"disambiguationData":[OSD([sQuery(id+"F26.wireOp",EDGE,"E186.MirrorCS")])],"isStart":true});
            fillet(context, id + "F28", {"entities" : qUnion([Q0]), "radius" : 12.7 * mm, "allowEdgeOverflow" : false});
        }
        {
            var Q0;
            Q0=makeQuery(id+"F27.opExtrude","CAP_EDGE",EDGE,{"disambiguationData":[OSD([sQuery(id+"F26.wireOp",EDGE,"E185")])],"isStart":true});
            fillet(context, id + "F29", {"entities" : qUnion([Q0]), "radius" : 12.7 * mm, "allowEdgeOverflow" : false});
        }
        {
            var Q0;
            Q0=makeQuery(id+"F27.opExtrude","CAP_EDGE",EDGE,{"disambiguationData":[OSD([sQuery(id+"F26.wireOp",EDGE,"E184")])],"isStart":true});
            var Q1;
            Q1=makeQuery(id+"F29.opFillet","BLEND_EDGE",EDGE,{"blendedFrom":[makeQuery(id+"F27.opExtrude","CAP_EDGE",EDGE,{"disambiguationData":[OSD([sQuery(id+"F26.wireOp",EDGE,"E185")])],"isStart":true}),makeQuery(id+"F27.opExtrude","SWEPT_FACE",FACE,{"disambiguationData":[OSD([sQuery(id+"F26.wireOp",EDGE,"E182")])]})],"blendedInto":[makeQuery(id+"F27.opExtrude","SWEPT_FACE",FACE,{"disambiguationData":[OSD([sQuery(id+"F26.wireOp",EDGE,"E182")])]})]});
            var Q2;
            Q2=makeQuery(id+"F27.opExtrude","CAP_EDGE",EDGE,{"disambiguationData":[OSD([sQuery(id+"F26.wireOp",EDGE,"E188.MirrorCS")])],"isStart":true});
            var Q3;
            Q3=makeQuery(id+"F28.opFillet","BLEND_EDGE",EDGE,{"blendedFrom":[makeQuery(id+"F27.opExtrude","CAP_EDGE",EDGE,{"disambiguationData":[OSD([sQuery(id+"F26.wireOp",EDGE,"E186.MirrorCS")])],"isStart":true}),makeQuery(id+"F27.opExtrude","SWEPT_FACE",FACE,{"disambiguationData":[OSD([sQuery(id+"F26.wireOp",EDGE,"E187.MirrorCS")])]})],"blendedInto":[makeQuery(id+"F27.opExtrude","SWEPT_FACE",FACE,{"disambiguationData":[OSD([sQuery(id+"F26.wireOp",EDGE,"E187.MirrorCS")])]})]});
            fillet(context, id + "F30", {"entities" : qUnion([Q0, Q1, Q2, Q3]), "radius" : 7.62 * mm, "tangentPropagation" : true, "allowEdgeOverflow" : false});
        }
        {
            var Q0;
            Q0=makeQuery(id+"F27.opExtrude","CAP_EDGE",EDGE,{"disambiguationData":[OSD([sQuery(id+"F26.wireOp",EDGE,"E186.MirrorCS")])],"isStart":false});
            var Q1;
            Q1=makeQuery(id+"F27.opExtrude","CAP_EDGE",EDGE,{"disambiguationData":[OSD([sQuery(id+"F26.wireOp",EDGE,"E185")])],"isStart":false});
            fillet(context, id + "F31", {"entities" : qUnion([Q0, Q1]), "radius" : 6.35 * mm, "tangentPropagation" : true, "allowEdgeOverflow" : false});
        }
        {
            var Q0;
            Q0=makeQuery(id+"F0.imprint","IMPRINT",FACE,{"disambiguationData":[TD([[makeQuery(id+"F0.imprint","IMPRINT",EDGE,{"derivedFrom":sQuery(id+"F0.wireOp",EDGE,"E23")}),1.0]])]});
            cPlane(context, id + "F32", {"entities" : qUnion([Q0]), "cplaneType" : CPlaneType.OFFSET, "offset" : 19.05 * mm, "oppositeDirection" : true, "width" : 152.4 * mm, "height" : 152.4 * mm});
        }
        {
            var Q0;
            Q0=makeQuery(id+"F3.opExtrude","SWEPT_FACE",FACE,{"disambiguationData":[OSD([sQuery(id+"F2.wireOp",EDGE,"E65")])]});
            cPlane(context, id + "F33", {"entities" : qUnion([Q0]), "cplaneType" : CPlaneType.OFFSET, "offset" : 0 * mm, "width" : 152.4 * mm, "height" : 152.4 * mm});
        }
        {
            var Q0;
            Q0=makeQuery(id+"F3.opExtrude","SWEPT_FACE",FACE,{"disambiguationData":[OSD([sQuery(id+"F2.wireOp",EDGE,"E65")])]});
            cPlane(context, id + "F34", {"entities" : qUnion([Q0]), "cplaneType" : CPlaneType.OFFSET, "offset" : 38.1 * mm, "width" : 152.4 * mm, "height" : 152.4 * mm});
        }
        {
            var Q0;
            Q0=makeQuery(id+"F3.opExtrude","SWEPT_FACE",FACE,{"disambiguationData":[OSD([sQuery(id+"F2.wireOp",EDGE,"E66")])]});
            cPlane(context, id + "F35", {"entities" : qUnion([Q0]), "cplaneType" : CPlaneType.OFFSET, "offset" : 0 * mm, "width" : 152.4 * mm, "height" : 152.4 * mm});
        }
        {
            var Q0;
            Q0=makeQuery(id+"F3.opExtrude","SWEPT_FACE",FACE,{"disambiguationData":[OSD([sQuery(id+"F2.wireOp",EDGE,"E66")])]});
            cPlane(context, id + "F36", {"entities" : qUnion([Q0]), "cplaneType" : CPlaneType.OFFSET, "offset" : 50.8 * mm, "width" : 152.4 * mm, "height" : 152.4 * mm});
        }
    });
